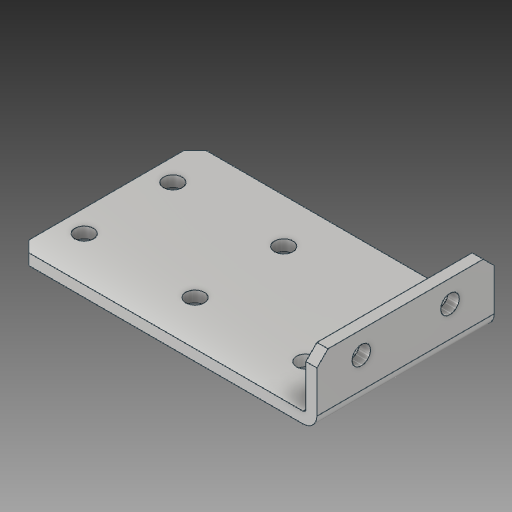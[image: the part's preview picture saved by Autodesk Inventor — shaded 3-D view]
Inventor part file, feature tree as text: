
AUTODESK INVENTOR PART (.ipt)
format: ipt  version: 2017.1 (Build 211199000, 199)  size: 128,512 bytes
history: native  units: in
note: dims shown in document units (in); Inventor stores cm internally (conversion verified against a paired STEP export)
features: chamfer x1
ambient origin geometry x8: Origin, YZ Plane, XZ Plane, XY Plane, X Axis, Y Axis, Z Axis, Center Point
bodies: Solid1 (feature_tree)
feature tree (1):
  chamfer  "Chamfer2"  [1 undecoded]
note: 1 required parameter value undecoded (feature->parameter linkage not recoverable at this tier; creation-order binding heuristic only, values carry confidence <= 0.55)
